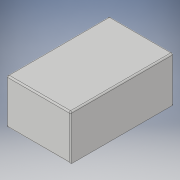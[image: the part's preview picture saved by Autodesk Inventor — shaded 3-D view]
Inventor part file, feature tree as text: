
AUTODESK INVENTOR PART (.ipt)
format: ipt  version: 2018 (Build 220112000, 112)  size: 103,936 bytes
history: native  units: in
note: dims shown in document units (in); Inventor stores cm internally (conversion verified against a paired STEP export)
features: extrude x1, fillet x1, sketch x1
ambient origin geometry x8: Origin, YZ Plane, XZ Plane, XY Plane, X Axis, Y Axis, Z Axis, Center Point
bodies: Solid1 (feature_tree)
feature tree (3):
  extrude  "Extrusion1"  Depth=5.9449in
  fillet  "Fillet1"  Radius=2.5984in
  sketch  "Sketch1"  dims[d0=3.7008in d1=5.9449in d2=2.5984in d3=0.0in d4=0.0787in]
